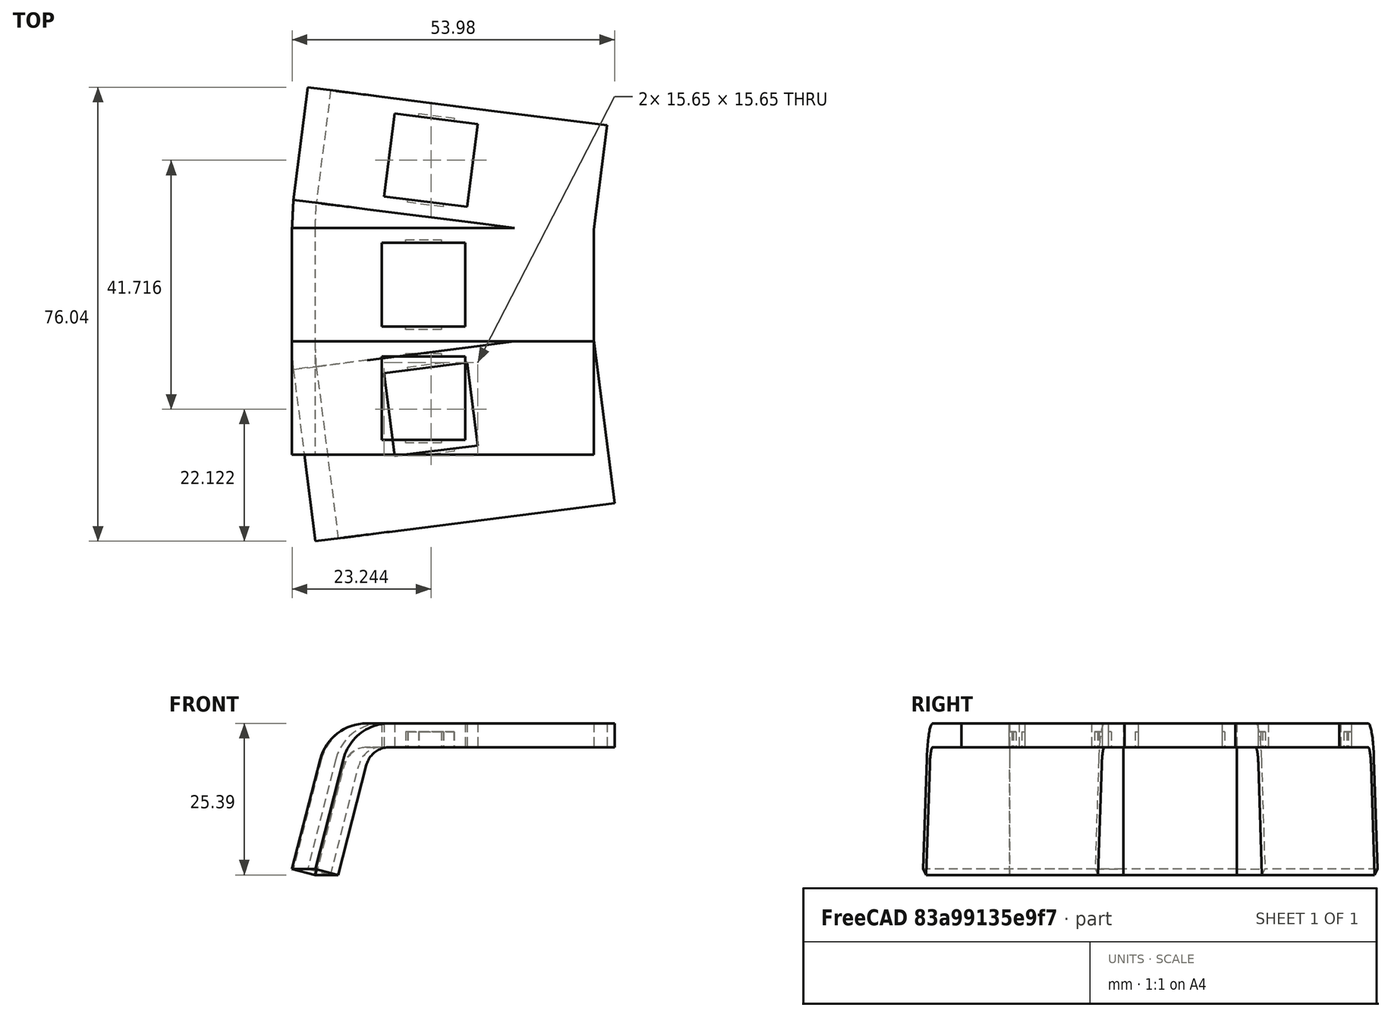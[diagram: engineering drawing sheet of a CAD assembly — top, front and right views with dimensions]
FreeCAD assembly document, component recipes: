
FREECAD ASSEMBLY — COMPONENT RECIPES ("KeyRowThumb2")

This assembly document has 5 components, labeled P0..P4 below (a component is one placed body or linked part). 4 of them carry a construction recipe — the FreeCAD feature program that regenerates the part from scratch, quoted from this document or its linked companion documents; the rest are supplied as boundary geometry only. No exploded tour is included for this assembly.
COMPONENT P0 — recipe-attached ("Body", modeled in this document).
Construction recipe (the document's own serialized feature program — sketch geometry with constraints, then the solid features built on it; lengths are millimeters unless a unit is written):

FEATURE [Sketcher::SketchObject] Sketch
  FullyConstrained = false
  MapMode = 5
  Placement = pos=(0,0,0) rot=(1,0,0;1.5708rad)
  Support = -> [XZ_Plane]
  sketch-geometry (15):
    g0: LineSegment StartX=-9.5 StartY=2 StartZ=0 EndX=9.5 EndY=2 EndZ=0
    g1: LineSegment StartX=9.5 StartY=2 StartZ=0 EndX=9.5 EndY=-2 EndZ=0
    g2: LineSegment StartX=9.5 StartY=-2 StartZ=0 EndX=-9.5 EndY=-2 EndZ=0
    g3: LineSegment StartX=-9.5 StartY=-2 StartZ=0 EndX=-9.5 EndY=2 EndZ=0
    g4: LineSegment StartX=-17.2452 StartY=-3.99696 StartZ=0 EndX=-13.3726 EndY=-4.99848 EndZ=0
    g5: LineSegment StartX=-9.5 StartY=-2 StartZ=0 EndX=-9.5 EndY=-6 EndZ=0
    g6: LineSegment StartX=-17.2452 StartY=-3.99696 StartZ=0 EndX=-22.0024 EndY=-22.3918 EndZ=0
    g7: LineSegment StartX=-22.0024 StartY=-22.3918 StartZ=0 EndX=-18.1298 EndY=-23.3933 EndZ=0
    g8: LineSegment StartX=-18.1298 StartY=-23.3933 StartZ=0 EndX=-13.3726 EndY=-4.99848 EndZ=0
    g9: LineSegment StartX=9.5 StartY=2 StartZ=0 EndX=28.5 EndY=2 EndZ=0
    g10: LineSegment StartX=28.5 StartY=2 StartZ=0 EndX=28.5 EndY=-2 EndZ=0
    g11: LineSegment StartX=28.5 StartY=-2 StartZ=0 EndX=9.5 EndY=-2 EndZ=0
    g12: LineSegment StartX=9.5 StartY=-21 StartZ=0 EndX=9.5 EndY=-2 EndZ=0
    g13: ArcOfCircle CenterX=-9.5 CenterY=-6 CenterZ=0 NormalX=0 NormalY=0 NormalZ=1 AngleXU=0 Radius=4 StartAngle=1.5708 EndAngle=2.88852
    g14: ArcOfCircle CenterX=-9.5 CenterY=-6 CenterZ=0 NormalX=0 NormalY=0 NormalZ=1 AngleXU=0 Radius=8 StartAngle=1.5708 EndAngle=2.88852
  constraints (36):
    c: Coincident(g1,g2)
    c: Coincident(g2,g3)
    c: Coincident(g3,g0)
    c: Horizontal(g0)
    c: Horizontal(g2)
    c: Vertical(g1)
    c: Symmetric(g0,g1,g-1)
    c: DistanceX(g0,g0) = 19
    c: DistanceY(g1,g1) = 4
    c: Distance(g4) = 4
    c: Coincident(g5,g2)
    c: Coincident(g4,g6) = -1.5708
    c: Coincident(g6,g7)
    c: Coincident(g7,g8)
    c: Distance(g5) = 4
    c: Coincident(g10,g9)
    c: Coincident(g11,g10)
    c: Perpendicular(g11,g10)
    c: Perpendicular(g9,g10)
    c: Distance(g10) = 4
    c: Distance(g9) = 19
    c: Coincident(g12,g2)
    c: Vertical(g12)
    c: Distance(g12) = 19
    c: Perpendicular(g7,g8)
    c: Perpendicular(g6,g7)
    c: Distance(g8) = 19
    c: Angle(g8,g2) = 1.82387
    c: Coincident(g0,g9)
    c: Coincident(g11,g2)
    c: Vertical(g1,g0)
    c: Coincident(g14,g13)
    c: Tangent(g13,g8) = 1.5708
    c: Tangent(g14,g6) = -1.5708
    c: Tangent(g14,g0) = 1.5708
    c: Tangent(g13,g2) = -1.5708
FEATURE [PartDesign::Pad] Pad
  Direction = (0,-1,-2e-16)
  Length = 19
  Length2 = 10
  Midplane = true
  Placement = pos=(0,0,0) rot=(1,0,0;1.5708rad)
  Profile = -> Sketch
  ReferenceAxis = -> Sketch [N_Axis]
  Type = 0
FEATURE [PartDesign::Body] Body
  Group = -> [Sketch,Pad]
  Origin = -> Origin
  Tip = -> Pad
COMPONENT P1 — recipe-attached ("Body002", modeled in this document).
Construction recipe (the document's own serialized feature program — sketch geometry with constraints, then the solid features built on it; lengths are millimeters unless a unit is written):

FEATURE [Sketcher::SketchObject] Sketch003
  FullyConstrained = false
  Placement = pos=(0,28.5,6e-15) rot=(-1,0,0;1.5708rad)
  sketch-geometry (10):
    g0: ArcOfCircle CenterX=-9.5 CenterY=6 CenterZ=0 NormalX=0 NormalY=1e-16 NormalZ=1 AngleXU=-1.5708 Radius=8 StartAngle=3.39467 EndAngle=4.71239
    g1: LineSegment StartX=-9.5 StartY=-2 StartZ=0 EndX=9.5 EndY=-2 EndZ=0
    g2: LineSegment StartX=9.5 StartY=-2 StartZ=0 EndX=15.2461 EndY=-2 EndZ=0
    g3: LineSegment StartX=15.2461 StartY=-2 StartZ=0 EndX=15.2461 EndY=2 EndZ=0
    g4: LineSegment StartX=15.2461 StartY=2 StartZ=0 EndX=9.5 EndY=2 EndZ=0
    g5: LineSegment StartX=9.5 StartY=2 StartZ=0 EndX=-9.5 EndY=2 EndZ=0
    g6: ArcOfCircle CenterX=-9.5 CenterY=6 CenterZ=0 NormalX=0 NormalY=1e-16 NormalZ=1 AngleXU=-1.5708 Radius=4 StartAngle=3.39467 EndAngle=4.71239
    g7: LineSegment StartX=-18.1298 StartY=23.3933 StartZ=0 EndX=-13.3726 EndY=4.99848 EndZ=0
    g8: LineSegment StartX=-22.0024 StartY=22.3918 StartZ=0 EndX=-18.1298 EndY=23.3933 EndZ=0
    g9: LineSegment StartX=-17.2452 StartY=3.99696 StartZ=0 EndX=-22.0024 EndY=22.3918 EndZ=0
  constraints (15):
    c: Coincident(g0,g1)
    c: Horizontal(g1)
    c: Coincident(g1,g2)
    c: Horizontal(g2)
    c: Coincident(g2,g3)
    c: Vertical(g3)
    c: Coincident(g3,g4)
    c: Horizontal(g4)
    c: Coincident(g4,g5)
    c: Horizontal(g5)
    c: Coincident(g5,g6)
    c: Coincident(g6,g7)
    c: Coincident(g7,g8)
    c: Coincident(g8,g9)
    c: Coincident(g9,g0)
FEATURE [Sketcher::SketchObject] Sketch004
  FullyConstrained = false
  Placement = pos=(3.81073,29.9548,-3.16e-13) rot=(0.992005,-0.126199,0;1.5708rad)
  sketch-geometry (10):
    g0: ArcOfCircle CenterX=-13.9465 CenterY=-4.27414 CenterZ=0 NormalX=0 NormalY=-1e-16 NormalZ=1 AngleXU=-1.69733 Radius=8 StartAngle=1.5708 EndAngle=2.88852
    g1: LineSegment StartX=-21.3769 StartY=-1.30968 StartZ=0 EndX=-28.4175 EndY=-18.9571 EndZ=0
    g2: LineSegment StartX=-28.4175 StartY=-18.9571 StartZ=0 EndX=-24.7023 EndY=-20.4393 EndZ=0
    g3: LineSegment StartX=-24.7023 StartY=-20.4393 StartZ=0 EndX=-17.6617 EndY=-2.79191 EndZ=0
    g4: ArcOfCircle CenterX=-13.9465 CenterY=-4.27414 CenterZ=0 NormalX=0 NormalY=-1e-16 NormalZ=1 AngleXU=-1.69733 Radius=4 StartAngle=1.5708 EndAngle=2.88852
    g5: LineSegment StartX=5.40643 StartY=-2.7039 StartZ=0 EndX=-13.4417 EndY=-0.306123 EndZ=0
    g6: LineSegment StartX=11.183 StartY=-3.43878 StartZ=0 EndX=5.40643 EndY=-2.7039 EndZ=0
    g7: LineSegment StartX=11.6878 StartY=0.529244 StartZ=0 EndX=11.183 EndY=-3.43878 EndZ=0
    g8: LineSegment StartX=5.91123 StartY=1.26412 StartZ=0 EndX=11.6878 EndY=0.529244 EndZ=0
    g9: LineSegment StartX=-12.9369 StartY=3.6619 StartZ=0 EndX=5.91123 EndY=1.26412 EndZ=0
  constraints (10):
    c: Coincident(g0,g1)
    c: Coincident(g1,g2)
    c: Coincident(g2,g3)
    c: Coincident(g3,g4)
    c: Coincident(g4,g5)
    c: Coincident(g5,g6)
    c: Coincident(g6,g7)
    c: Coincident(g7,g8)
    c: Coincident(g8,g9)
    c: Coincident(g9,g0)
FEATURE [PartDesign::AdditiveLoft] AdditiveLoft001
  Closed = false
  Placement = pos=(0,28.5,6e-15) rot=(-1,0,0;1.5708rad)
  Profile = -> Sketch003
  Ruled = false
  Sections = -> [Sketch004]
FEATURE [PartDesign::Body] Body002
  Group = -> [Sketch003,Sketch004,AdditiveLoft001]
  Origin = -> Origin002
  Tip = -> AdditiveLoft001
COMPONENT P2 — recipe-attached ("Body003", modeled in this document).
Construction recipe (the document's own serialized feature program — sketch geometry with constraints, then the solid features built on it; lengths are millimeters unless a unit is written):

FEATURE [PartDesign::SubShapeBinder] Binder
  BindCopyOnChange = 0
  BindMode = 0
  ClaimChildren = false
  Context = -> Body003 [Binder.]
  Fuse = false
  MakeFace = true
  OffsetFill = false
  OffsetIntersection = false
  OffsetJoinType = 0
  OffsetOpenResult = false
  PartialLoad = false
  Relative = true
  Support = -> [Link001[Face3]]
  _Version = 2
FEATURE [PartDesign::Pad] Pad001
  Direction = (0.126199,-0.992005,-2e-16)
  Length = 10
  Length2 = 10
  Profile = -> Binder
  Type = 0
FEATURE [PartDesign::Body] Body003
  Group = -> [Binder,Pad001]
  Origin = -> Origin003
  Tip = -> Pad001
COMPONENT P3 — recipe-attached ("MX-Latch-SubtractorNice", modeled in this document).
Construction recipe (the document's own serialized feature program — sketch geometry with constraints, then the solid features built on it; lengths are millimeters unless a unit is written):

FEATURE [Sketcher::SketchObject] Sketch005
  FullyConstrained = false
  Placement = pos=(-0.946492,7.44004,2e-15) rot=(-0.992005,-0.126199,0;1.5708rad)
  sketch-geometry (10):
    g0: ArcOfCircle CenterX=-9.18924 CenterY=4.87934 CenterZ=0 NormalX=0 NormalY=1e-16 NormalZ=1 AngleXU=-1.44426 Radius=8 StartAngle=3.39467 EndAngle=4.71239
    g1: LineSegment StartX=-8.17964 StartY=-3.0567 StartZ=0 EndX=10.6685 EndY=-0.65892 EndZ=0
    g2: LineSegment StartX=10.6685 StartY=-0.65892 StartZ=0 EndX=16.445 EndY=0.0759518 EndZ=0
    g3: LineSegment StartX=16.445 StartY=0.0759518 StartZ=0 EndX=15.9402 EndY=4.04397 EndZ=0
    g4: LineSegment StartX=15.9402 StartY=4.04397 StartZ=0 EndX=10.1637 EndY=3.3091 EndZ=0
    g5: LineSegment StartX=10.1637 StartY=3.3091 StartZ=0 EndX=-8.68444 EndY=0.911319 EndZ=0
    g6: ArcOfCircle CenterX=-9.18924 CenterY=4.87934 CenterZ=0 NormalX=0 NormalY=1e-16 NormalZ=1 AngleXU=-1.44426 Radius=4 StartAngle=3.39467 EndAngle=4.71239
    g7: LineSegment StartX=-19.9451 StartY=21.0445 StartZ=0 EndX=-12.9045 EndY=3.39711 EndZ=0
    g8: LineSegment StartX=-23.6603 StartY=19.5623 StartZ=0 EndX=-19.9451 EndY=21.0445 EndZ=0
    g9: LineSegment StartX=-16.6197 StartY=1.91488 StartZ=0 EndX=-23.6603 EndY=19.5623 EndZ=0
  constraints (10):
    c: Coincident(g0,g1)
    c: Coincident(g1,g2)
    c: Coincident(g2,g3)
    c: Coincident(g3,g4)
    c: Coincident(g4,g5)
    c: Coincident(g5,g6)
    c: Coincident(g6,g7)
    c: Coincident(g7,g8)
    c: Coincident(g8,g9)
    c: Coincident(g9,g0)
FEATURE [Sketcher::SketchObject] Sketch006
  FullyConstrained = false
  Placement = pos=(0,9.5,2e-15) rot=(1,0,0;1.5708rad)
  sketch-geometry (10):
    g0: ArcOfCircle CenterX=-9.5 CenterY=-6 CenterZ=0 NormalX=0 NormalY=0 NormalZ=1 AngleXU=0 Radius=8 StartAngle=1.5708 EndAngle=2.88852
    g1: LineSegment StartX=-17.2452 StartY=-3.99696 StartZ=0 EndX=-22.0024 EndY=-22.3918 EndZ=0
    g2: LineSegment StartX=-22.0024 StartY=-22.3918 StartZ=0 EndX=-18.1298 EndY=-23.3933 EndZ=0
    g3: LineSegment StartX=-18.1298 StartY=-23.3933 StartZ=0 EndX=-13.3726 EndY=-4.99848 EndZ=0
    g4: ArcOfCircle CenterX=-9.5 CenterY=-6 CenterZ=0 NormalX=0 NormalY=0 NormalZ=1 AngleXU=0 Radius=4 StartAngle=1.5708 EndAngle=2.88852
    g5: LineSegment StartX=9.5 StartY=-2 StartZ=0 EndX=-9.5 EndY=-2 EndZ=0
    g6: LineSegment StartX=15.2461 StartY=-2 StartZ=0 EndX=9.5 EndY=-2 EndZ=0
    g7: LineSegment StartX=15.2461 StartY=2 StartZ=0 EndX=15.2461 EndY=-2 EndZ=0
    g8: LineSegment StartX=9.5 StartY=2 StartZ=0 EndX=15.2461 EndY=2 EndZ=0
    g9: LineSegment StartX=-9.5 StartY=2 StartZ=0 EndX=9.5 EndY=2 EndZ=0
  constraints (15):
    c: Coincident(g0,g1)
    c: Coincident(g1,g2)
    c: Coincident(g2,g3)
    c: Coincident(g3,g4)
    c: Coincident(g4,g5)
    c: Horizontal(g5)
    c: Coincident(g5,g6)
    c: Horizontal(g6)
    c: Coincident(g6,g7)
    c: Vertical(g7)
    c: Coincident(g7,g8)
    c: Horizontal(g8)
    c: Coincident(g8,g9)
    c: Horizontal(g9)
    c: Coincident(g9,g0)
FEATURE [PartDesign::AdditiveLoft] AdditiveLoft
  Closed = false
  Placement = pos=(-0.946492,7.44004,2e-15) rot=(-0.992005,-0.126199,0;1.5708rad)
  Profile = -> Sketch005
  Ruled = false
  Sections = -> [Sketch006]
FEATURE [PartDesign::Body] Body001
  Group = -> [Sketch005,Sketch006,AdditiveLoft]
  Origin = -> Origin001
  Tip = -> AdditiveLoft
COMPONENT P4 — geometry summary ("Cut003"; no construction recipe available for this part):
  bounding box: 52.5 x 25.4 x 25.2 mm
  tessellated surface: 296 triangles
  volume: 4133 mm^3 (12% of its bounding box)
PROVENANCE & LICENSES
A FreeCAD (.FCStd) document from a public repository crawl; recipes are the document's own serialized feature recipes (and, for linked parts, companion documents' recipes).
License: mit.
